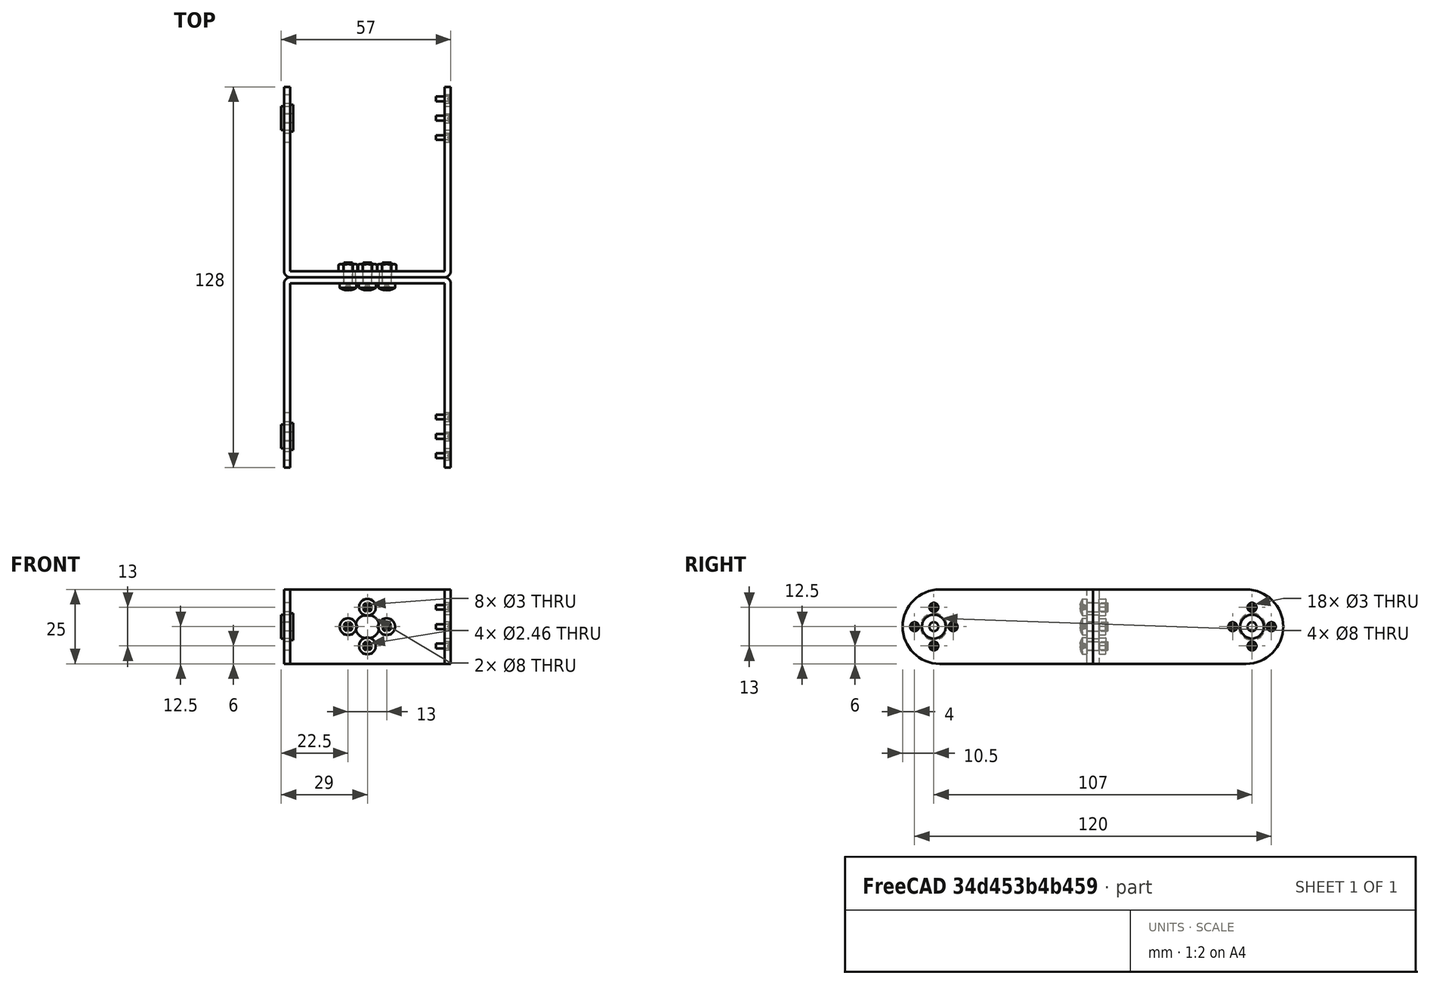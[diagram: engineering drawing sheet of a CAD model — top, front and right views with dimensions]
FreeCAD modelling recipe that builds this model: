
FCSTD DOCUMENT  (FreeCAD 0.19R24276 (Git))
Label: cuerpo
License: All rights reserved
LicenseURL: http://en.wikipedia.org/wiki/All_rights_reserved
objects: Part::FeaturePython×20, App::FeaturePython×14, App::DocumentObjectGroup×4
note: 20 computed .brp shape members not serialized (recipe doc carries the construction recipe); baked Part::Feature solids carry a one-line shape summary decoded from their .brp

FEATURE [Part::FeaturePython] b_parte_union_001_  label="parte_union_001"  # a2plus imported part (geometry in sourceFile) (typed FeaturePython)
  Placement = pos=(0,0,0) rot=(1,0,0;1.5708rad)
  a2p_Version = V0.1
  fixedPosition = true
  objectType = a2pPart
  sourceFile = .\..\piezas\parte_union.FCStd
  subassemblyImport = false
  timeLastImport = 1.62041e+09
  updateColors = true
FEATURE [Part::FeaturePython] b_parte_union_001_001  label="parte_union_002"  # a2plus imported part (geometry in sourceFile) (typed FeaturePython)
  Placement = pos=(1.53312e-08,4e-14,1.42954e-08) rot=(-1,0,0;1.5708rad)
  a2p_Version = V0.1
  fixedPosition = false
  objectType = a2pPart
  sourceFile = .\..\piezas\parte_union.FCStd
  subassemblyImport = false
  timeLastImport = 1.62041e+09
  updateColors = true
FEATURE [Part::FeaturePython] b_arandela_001_  label="arandela_001"  # a2plus imported part (geometry in sourceFile) (typed FeaturePython)
  Placement = pos=(-25,-53.5,3.75599e-09) rot=(0,-1,0;1.5708rad)
  a2p_Version = V0.1
  fixedPosition = false
  objectType = a2pPart
  sourceFile = .\..\piezas\arandela.FCStd
  subassemblyImport = false
  timeLastImport = 1.62041e+09
  updateColors = true
FEATURE [App::FeaturePython] planeCoincident_001  label="planeCoincident_001__parte_union_002"  # a2plus constraint (typed FeaturePython)
  Object1 = b_parte_union_001_
  Object2 = b_parte_union_001_001
  ParentTreeObject = -> b_parte_union_001_
  SubElement1 = Face5
  SubElement2 = Face5
  Suppressed = false
  Type = plane
  directionConstraint = 1
  offset = 0
FEATURE [App::FeaturePython] planeCoincident_001_mirror  label="planeCoincident_001__parte_union_001"  # a2plus constraint (typed FeaturePython)
  Object1 = b_parte_union_001_
  Object2 = b_parte_union_001_001
  ParentTreeObject = -> b_parte_union_001_001
  SubElement1 = Face5
  SubElement2 = Face5
  Suppressed = false
  Type = plane
  directionConstraint = 1
  offset = 0
FEATURE [App::FeaturePython] axisCoincident_001  label="axisCoincident_001__parte_union_001"  # a2plus constraint (typed FeaturePython)
  Object1 = b_parte_union_001_001
  Object2 = b_parte_union_001_
  ParentTreeObject = -> b_parte_union_001_001
  SubElement1 = Face16
  SubElement2 = Face16
  Suppressed = false
  Type = axial
  directionConstraint = 1
  lockRotation = false
FEATURE [App::FeaturePython] axisCoincident_001_mirror  label="axisCoincident_001__parte_union_002"  # a2plus constraint (typed FeaturePython)
  Object1 = b_parte_union_001_001
  Object2 = b_parte_union_001_
  ParentTreeObject = -> b_parte_union_001_
  SubElement1 = Face16
  SubElement2 = Face16
  Suppressed = false
  Type = axial
  directionConstraint = 1
  lockRotation = false
FEATURE [App::FeaturePython] axisCoincident_002  label="axisCoincident_002__parte_union_002"  # a2plus constraint (typed FeaturePython)
  Object1 = b_parte_union_001_
  Object2 = b_parte_union_001_001
  ParentTreeObject = -> b_parte_union_001_
  SubElement1 = Face15
  SubElement2 = Face15
  Suppressed = false
  Type = axial
  directionConstraint = 1
  lockRotation = false
FEATURE [App::FeaturePython] axisCoincident_002_mirror  label="axisCoincident_002__parte_union_001"  # a2plus constraint (typed FeaturePython)
  Object1 = b_parte_union_001_
  Object2 = b_parte_union_001_001
  ParentTreeObject = -> b_parte_union_001_001
  SubElement1 = Face15
  SubElement2 = Face15
  Suppressed = false
  Type = axial
  directionConstraint = 1
  lockRotation = false
FEATURE [App::FeaturePython] planeCoincident_002  label="planeCoincident_002__parte_union_001"  # a2plus constraint (typed FeaturePython)
  Object1 = b_arandela_001_
  Object2 = b_parte_union_001_
  ParentTreeObject = -> b_arandela_001_
  SubElement1 = Face3
  SubElement2 = Face12
  Suppressed = false
  Type = plane
  directionConstraint = 0
  offset = 0
FEATURE [App::FeaturePython] planeCoincident_002_mirror  label="planeCoincident_002__arandela_001"  # a2plus constraint (typed FeaturePython)
  Object1 = b_arandela_001_
  Object2 = b_parte_union_001_
  ParentTreeObject = -> b_parte_union_001_
  SubElement1 = Face3
  SubElement2 = Face12
  Suppressed = false
  Type = plane
  directionConstraint = 0
  offset = 0
FEATURE [App::FeaturePython] axisCoincident_003  label="axisCoincident_003__parte_union_001"  # a2plus constraint (typed FeaturePython)
  Object1 = b_arandela_001_
  Object2 = b_parte_union_001_
  ParentTreeObject = -> b_arandela_001_
  SubElement1 = Face5
  SubElement2 = Face28
  Suppressed = false
  Type = axial
  directionConstraint = 0
  lockRotation = false
FEATURE [App::FeaturePython] axisCoincident_003_mirror  label="axisCoincident_003__arandela_001"  # a2plus constraint (typed FeaturePython)
  Object1 = b_arandela_001_
  Object2 = b_parte_union_001_
  ParentTreeObject = -> b_parte_union_001_
  SubElement1 = Face5
  SubElement2 = Face28
  Suppressed = false
  Type = axial
  directionConstraint = 0
  lockRotation = false
FEATURE [Part::FeaturePython] Screw  label="M3x7-Screw"  # Fasteners workbench fastener (typed FeaturePython)
  Placement = pos=(0,-2,6.5) rot=(1,0,0;1.5708rad)
  baseObject = -> b_parte_union_001_ [Edge31]
  diameter = 4
  invert = false
  length = 11
  lengthCustom = 7
  matchOuter = true
  offset = 0
  thread = false
  type = 34
FEATURE [Part::FeaturePython] Screw001  label="M3x7-Screw004"  # Fasteners workbench fastener (typed FeaturePython)
  Placement = pos=(-6.5,-2,4e-16) rot=(1,0,0;1.5708rad)
  baseObject = -> b_parte_union_001_ [Edge30]
  diameter = 4
  invert = false
  length = 11
  lengthCustom = 7
  matchOuter = true
  offset = 0
  thread = false
  type = 34
FEATURE [Part::FeaturePython] Screw002  label="M3x7-Screw005"  # Fasteners workbench fastener (typed FeaturePython)
  Placement = pos=(0,-2,-6.5) rot=(1,0,0;1.5708rad)
  baseObject = -> b_parte_union_001_ [Edge27]
  diameter = 4
  invert = false
  length = 11
  lengthCustom = 7
  matchOuter = true
  offset = 0
  thread = false
  type = 34
FEATURE [Part::FeaturePython] Screw003  label="M3x7-Screw006"  # Fasteners workbench fastener (typed FeaturePython)
  Placement = pos=(6.5,-2,4e-16) rot=(1,0,0;1.5708rad)
  baseObject = -> b_parte_union_001_ [Edge28]
  diameter = 4
  invert = false
  length = 11
  lengthCustom = 7
  matchOuter = true
  offset = 0
  thread = false
  type = 34
FEATURE [Part::FeaturePython] Screw004  label="M1.6x5-Screw"  # Fasteners workbench fastener (typed FeaturePython)
  Placement = pos=(28,-53.5,-6.5) rot=(0,1,0;1.5708rad)
  baseObject = -> b_parte_union_001_ [Edge80]
  diameter = 1
  invert = false
  length = 9
  lengthCustom = 5
  matchOuter = false
  offset = 0
  thread = false
  type = 35
FEATURE [Part::FeaturePython] Screw005  label="M1.6x5-Screw012"  # Fasteners workbench fastener (typed FeaturePython)
  Placement = pos=(28,-60,1.33e-14) rot=(0,1,0;1.5708rad)
  baseObject = -> b_parte_union_001_ [Edge78]
  diameter = 1
  invert = false
  length = 9
  lengthCustom = 5
  matchOuter = false
  offset = 0
  thread = false
  type = 35
FEATURE [Part::FeaturePython] Screw006  label="M1.6x5-Screw014"  # Fasteners workbench fastener (typed FeaturePython)
  Placement = pos=(28,-47,1.04e-14) rot=(0,1,0;1.5708rad)
  baseObject = -> b_parte_union_001_ [Edge82]
  diameter = 1
  invert = false
  length = 9
  lengthCustom = 5
  matchOuter = false
  offset = 0
  thread = false
  type = 35
FEATURE [Part::FeaturePython] Screw007  label="M1.6x5-Screw013"  # Fasteners workbench fastener (typed FeaturePython)
  Placement = pos=(28,-53.5,6.5) rot=(0,1,0;1.5708rad)
  baseObject = -> b_parte_union_001_ [Edge79]
  diameter = 1
  invert = false
  length = 9
  lengthCustom = 5
  matchOuter = false
  offset = 0
  thread = false
  type = 35
FEATURE [App::DocumentObjectGroup] Group002  label="parte_1"
  Group = -> [Screw004,Screw005,Screw007,Screw006]
FEATURE [Part::FeaturePython] Screw008  label="M1.6x5-Screw008"  # Fasteners workbench fastener (typed FeaturePython)
  Placement = pos=(28,60,1.42954e-08) rot=(0,1,0;1.5708rad)
  baseObject = -> b_parte_union_001_001 [Edge78]
  diameter = 1
  invert = false
  length = 9
  lengthCustom = 5
  matchOuter = true
  offset = 0
  thread = false
  type = 35
FEATURE [Part::FeaturePython] Screw009  label="M1.6x5-Screw009"  # Fasteners workbench fastener (typed FeaturePython)
  Placement = pos=(28,53.5,6.5) rot=(0,1,0;1.5708rad)
  baseObject = -> b_parte_union_001_001 [Edge80]
  diameter = 1
  invert = false
  length = 9
  lengthCustom = 5
  matchOuter = true
  offset = 0
  thread = false
  type = 35
FEATURE [Part::FeaturePython] Screw010  label="M1.6x5-Screw010"  # Fasteners workbench fastener (typed FeaturePython)
  Placement = pos=(28,53.5,-6.5) rot=(0,1,0;1.5708rad)
  baseObject = -> b_parte_union_001_001 [Edge79]
  diameter = 1
  invert = false
  length = 9
  lengthCustom = 5
  matchOuter = true
  offset = 0
  thread = false
  type = 35
FEATURE [Part::FeaturePython] Screw011  label="M1.6x5-Screw011"  # Fasteners workbench fastener (typed FeaturePython)
  Placement = pos=(28,47,1.42954e-08) rot=(0,1,0;1.5708rad)
  baseObject = -> b_parte_union_001_001 [Edge82]
  diameter = 1
  invert = false
  length = 9
  lengthCustom = 5
  matchOuter = true
  offset = 0
  thread = false
  type = 35
FEATURE [App::DocumentObjectGroup] Group003  label="parte_2"
  Group = -> [Screw008,Screw009,Screw010,Screw011]
FEATURE [App::DocumentObjectGroup] Group  label="ttonrimllos"
  Group = -> [Group003,Screw001,Screw003,Group002,Screw,Screw002]
FEATURE [Part::FeaturePython] Nut  label="M3-Nut"  # Fasteners workbench fastener (typed FeaturePython)
  Placement = pos=(1.53312e-08,2,-6.5) rot=(-1,0,0;1.5708rad)
  baseObject = -> b_parte_union_001_001 [Edge31]
  diameter = 4
  invert = false
  matchOuter = true
  offset = 0
  thread = false
  type = 7
FEATURE [Part::FeaturePython] Nut001  label="M3-Nut004"  # Fasteners workbench fastener (typed FeaturePython)
  Placement = pos=(-6.5,2,1.42954e-08) rot=(-1,0,0;1.5708rad)
  baseObject = -> b_parte_union_001_001 [Edge30]
  diameter = 4
  invert = false
  matchOuter = true
  offset = 0
  thread = false
  type = 7
FEATURE [Part::FeaturePython] Nut002  label="M3-Nut005"  # Fasteners workbench fastener (typed FeaturePython)
  Placement = pos=(1.53312e-08,2,6.5) rot=(-1,0,0;1.5708rad)
  baseObject = -> b_parte_union_001_001 [Edge27]
  diameter = 4
  invert = false
  matchOuter = true
  offset = 0
  thread = false
  type = 7
FEATURE [Part::FeaturePython] Nut003  label="M3-Nut006"  # Fasteners workbench fastener (typed FeaturePython)
  Placement = pos=(6.5,2,1.42954e-08) rot=(-1,0,0;1.5708rad)
  baseObject = -> b_parte_union_001_001 [Edge28]
  diameter = 4
  invert = false
  matchOuter = true
  offset = 0
  thread = false
  type = 7
FEATURE [App::DocumentObjectGroup] Group001  label="tuercas"
  Group = -> [Nut,Nut001,Nut002,Nut003]
FEATURE [Part::FeaturePython] b_arandela_001_001  label="arandela_002"  # a2plus imported part (geometry in sourceFile) (typed FeaturePython)
  Placement = pos=(-25,53.5,-9.53843e-08) rot=(0,-1,0;1.5708rad)
  a2p_Version = V0.1
  fixedPosition = false
  objectType = a2pPart
  sourceFile = .\..\piezas\arandela.FCStd
  subassemblyImport = false
  timeLastImport = 1.62041e+09
  updateColors = true
FEATURE [App::FeaturePython] planeCoincident_003  label="planeCoincident_003__arandela_002"  # a2plus constraint (typed FeaturePython)
  Object1 = b_parte_union_001_001
  Object2 = b_arandela_001_001
  ParentTreeObject = -> b_parte_union_001_001
  SubElement1 = Face12
  SubElement2 = Face3
  Suppressed = false
  Type = plane
  directionConstraint = 0
  offset = 0
FEATURE [App::FeaturePython] planeCoincident_003_mirror  label="planeCoincident_003__parte_union_002"  # a2plus constraint (typed FeaturePython)
  Object1 = b_parte_union_001_001
  Object2 = b_arandela_001_001
  ParentTreeObject = -> b_arandela_001_001
  SubElement1 = Face12
  SubElement2 = Face3
  Suppressed = false
  Type = plane
  directionConstraint = 0
  offset = 0
FEATURE [App::FeaturePython] axisCoincident_004  label="axisCoincident_004__parte_union_002"  # a2plus constraint (typed FeaturePython)
  Object1 = b_arandela_001_001
  Object2 = b_parte_union_001_001
  ParentTreeObject = -> b_arandela_001_001
  SubElement1 = Face5
  SubElement2 = Face28
  Suppressed = false
  Type = axial
  directionConstraint = 0
  lockRotation = false
FEATURE [App::FeaturePython] axisCoincident_004_mirror  label="axisCoincident_004__arandela_002"  # a2plus constraint (typed FeaturePython)
  Object1 = b_arandela_001_001
  Object2 = b_parte_union_001_001
  ParentTreeObject = -> b_parte_union_001_001
  SubElement1 = Face5
  SubElement2 = Face28
  Suppressed = false
  Type = axial
  directionConstraint = 0
  lockRotation = false
